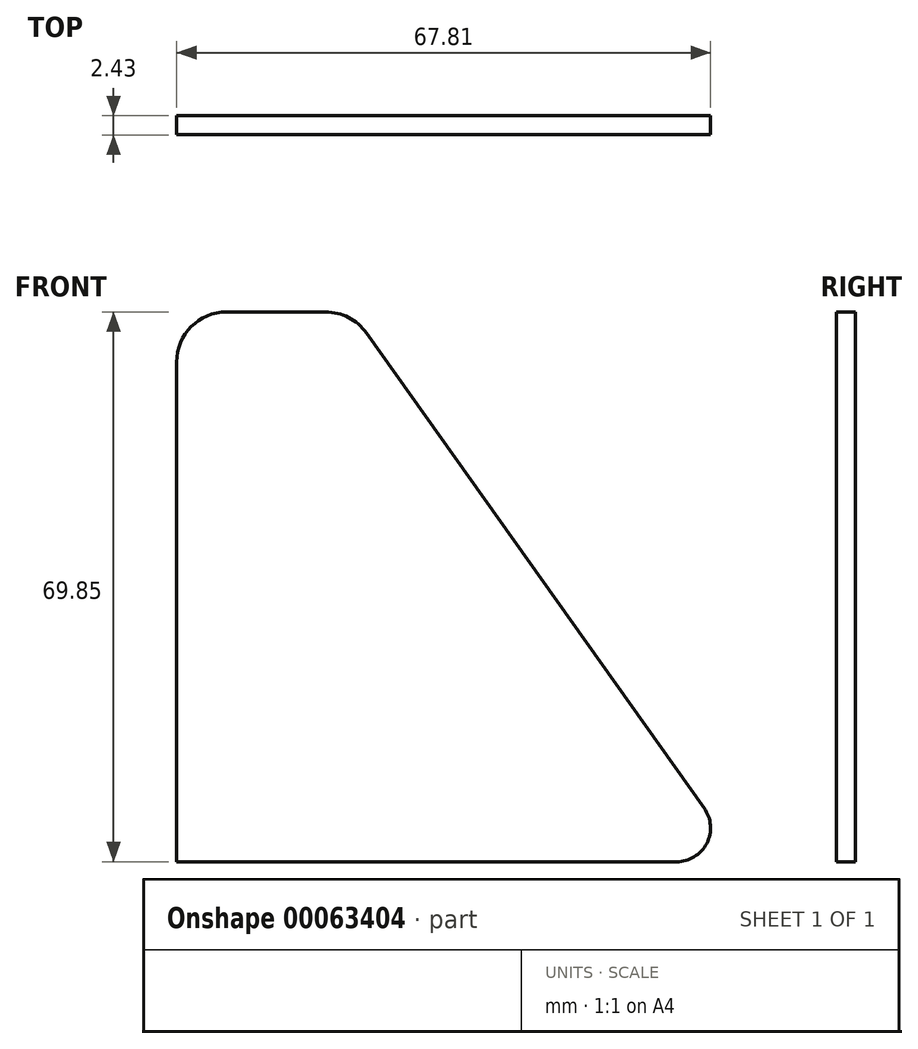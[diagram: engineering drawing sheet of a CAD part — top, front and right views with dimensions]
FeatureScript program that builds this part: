
annotation { "Feature Type Name" : "Feature", "Feature Type Description" : "" }
export const myFeature = defineFeature(function(context is Context, id is Id, definition is map)
    precondition{}
    {
        {
            var Q0;
            Q0=qCreatedBy(makeId("Front.planeOp"),FACE);
            var sketch = newSketch(context, id + "F0", { "sketchPlane" : qUnion([Q0])});
            skLineSegment(sketch, "E0", {"start": v(-38.32, -21.1) * mm, "end": v(-38.32, 42.4) * mm});
            skLineSegment(sketch, "E1", {"start": v(-31.97, 48.75) * mm, "end": v(-19.38, 48.75) * mm});
            skLineSegment(sketch, "E2", {"start": v(-14.2, 46.07) * mm, "end": v(28.7, -14.28) * mm});
            skLineSegment(sketch, "E3", {"start": v(25.18, -21.1) * mm, "end": v(-38.32, -21.1) * mm});
            skPoint(sketch, "E4.visualSharp", {"position": v(-38.32, 48.75) * mm});
            skArc(sketch, "E4.filletArc", {"start": v(-31.97, 48.75) * mm, "mid": v(-36.46, 46.89) * mm, "end": v(-38.32, 42.4) * mm});
            skPoint(sketch, "E5.visualSharp", {"position": v(-16.1, 48.75) * mm});
            skArc(sketch, "E5.filletArc", {"start": v(-14.2, 46.07) * mm, "mid": v(-16.47, 48.04) * mm, "end": v(-19.38, 48.75) * mm});
            skPoint(sketch, "E6.visualSharp", {"position": v(33.54, -21.1) * mm});
            skArc(sketch, "E6.filletArc", {"start": v(25.18, -21.1) * mm, "mid": v(29.01, -18.77) * mm, "end": v(28.7, -14.28) * mm});
            skSolve(sketch);
        }
        {
            var Q0;
            Q0=makeQuery(id+"F0.imprint","IMPRINT",FACE,{"disambiguationData":[TD([[makeQuery(id+"F0.imprint","IMPRINT",EDGE,{"derivedFrom":sQuery(id+"F0.wireOp",EDGE,"E0")}),-1.0]])]});
            extrude(context, id + "F1", {"entities" : qUnion([Q0]), "depth" : 2.43 * mm});
        }
    });
